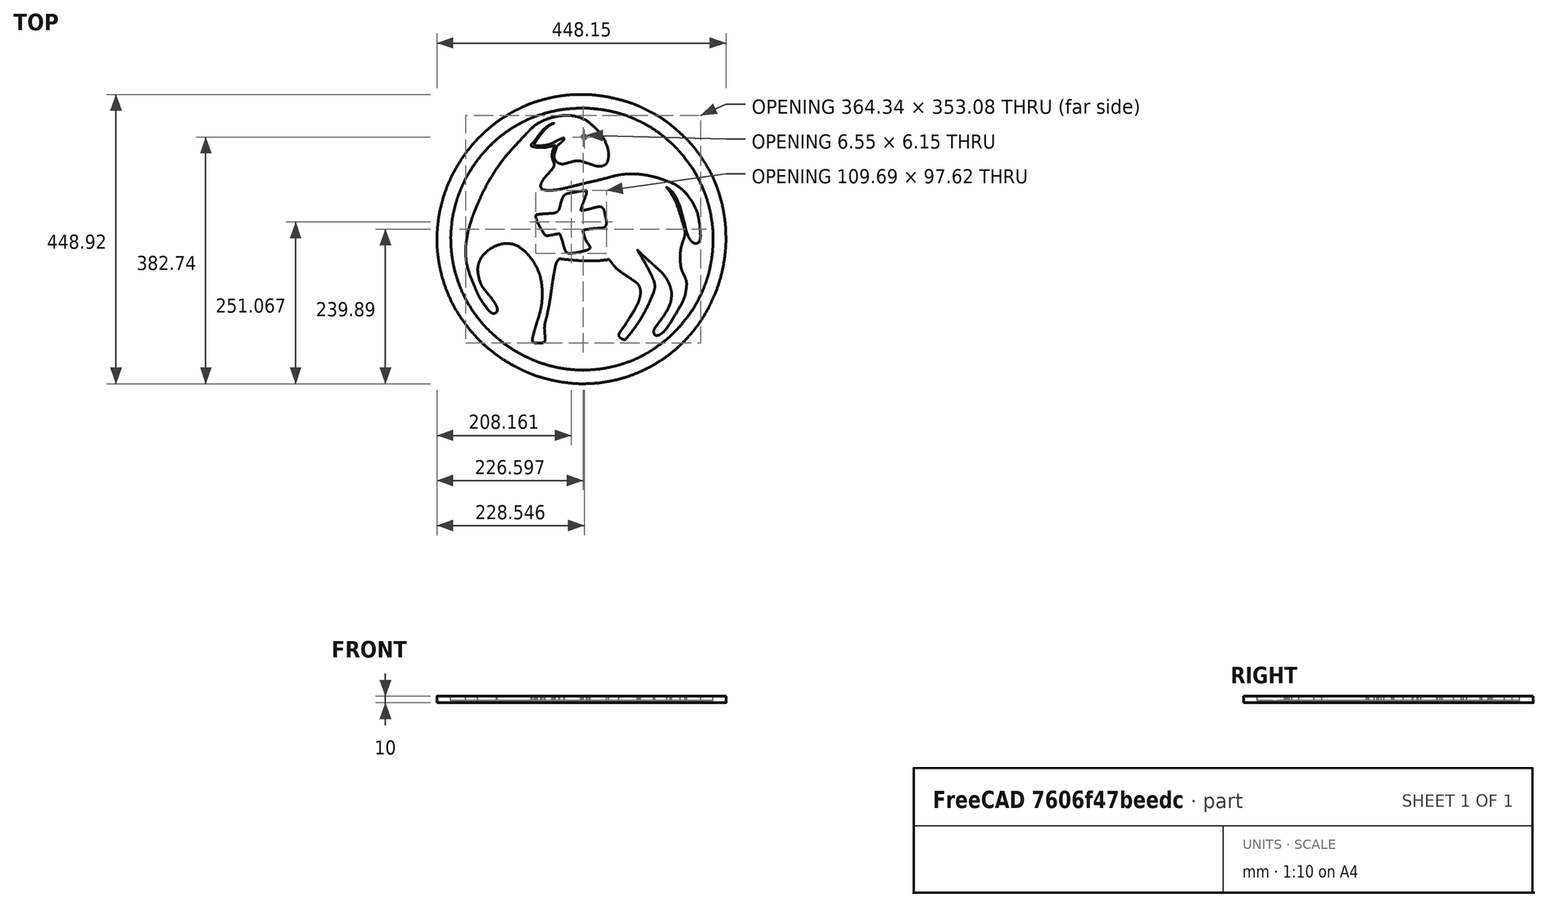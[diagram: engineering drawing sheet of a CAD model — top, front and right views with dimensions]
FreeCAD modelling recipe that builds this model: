
FCSTD DOCUMENT  (FreeCAD 0.16R6712 (Git))
Label: 2
License: All rights reserved
LicenseURL: http://en.wikipedia.org/wiki/All_rights_reserved
objects: Part::Feature×7, Part::Extrusion×5, Part::MultiFuse×3, Part::Cut×3
note: 18 computed .brp shape members not serialized (recipe doc carries the construction recipe); baked Part::Feature solids carry a one-line shape summary decoded from their .brp

FEATURE [Part::Feature] Path005
  shape: bbox 448.2 x 449 x 2e-07 mm, 0 faces, 0 solids (baked)
FEATURE [Part::Feature] Path007
  shape: bbox 407 x 406.8 x 2e-07 mm, 0 faces, 0 solids (baked)
FEATURE [Part::Feature] Path011
  shape: bbox 364.5 x 353.2 x 2e-07 mm, 0 faces, 0 solids (baked)
FEATURE [Part::Feature] Path021
  shape: bbox 109.9 x 98 x 2e-07 mm, 0 faces, 0 solids (baked)
FEATURE [Part::Feature] Path022
  shape: bbox 6.576 x 6.181 x 2e-07 mm, 0 faces, 0 solids (baked)
FEATURE [Part::MultiFuse] Fusion
  Shapes = -> [Path021,Path022]
FEATURE [Part::Extrusion] Extrude002
  Base = -> Fusion
  Dir = (0,0,30)
  Solid = true
FEATURE [Part::Extrusion] Extrude005
  Base = -> Path011
  Dir = (0,0,10)
  Solid = true
FEATURE [Part::Cut] Cut
  Base = -> Extrude005
  Tool = -> Extrude002
FEATURE [Part::Extrusion] Extrude007
  Base = -> Path005
  Dir = (0,0,10)
  Solid = true
FEATURE [Part::Extrusion] Extrude010
  Base = -> Path007
  Dir = (0,0,20)
  Placement = pos=(0,0,3) rot=(0,0,1;0rad)
  Solid = true
FEATURE [Part::Cut] Cut001
  Base = -> Extrude007
  Tool = -> Extrude010
FEATURE [Part::Feature] Path023
  shape: bbox 109.9 x 98 x 2e-07 mm, 0 faces, 0 solids (baked)
FEATURE [Part::Feature] Path024
  shape: bbox 6.576 x 6.181 x 2e-07 mm, 0 faces, 0 solids (baked)
FEATURE [Part::MultiFuse] Fusion001
  Shapes = -> [Path023,Path024]
FEATURE [Part::Extrusion] Extrude011
  Base = -> Fusion001
  Dir = (0,0,30)
  Placement = pos=(0,0,-9) rot=(0,0,1;0rad)
  Solid = true
FEATURE [Part::MultiFuse] Fusion002
  Shapes = -> [Cut001,Cut]
FEATURE [Part::Cut] Cut002
  Base = -> Fusion002
  Tool = -> Extrude011
